# Revit family: Toilet_Seat-Round_Closed_Front-KOHLER-Stonewood-K-4648
name_source: partatom
category: Specialty Equipment
revit_build: Autodesk Revit 2015 (Build: 20140606_1530(x64)
units: mm (PartAtom-declared; Revit-internal decimal feet)

## types (3) — shared parameters
ADA Compliant = No
Assembly Code = C1030200
Date Modified = 12/20/2019
Default Elevation = 0"
Description = Round-Front Toilet Seat
Height = 1 1/16"
Length = 16 5/8"
Manufacturer = KOHLER Co.
MasterFormat 1995 = 10820
MasterFormat 2004 = 10.28.13
Material = Molded Wood
Product Documentation Link = https://www.us.kohler.com
Product Name = Stonewood
Product Page URL = http://www.us.kohler.com
URL = https://www.us.kohler.com
WaterSense Certified = No
Width = 14 3/16"

## per-type parameters (varying)
| type | Finish | Model | Type |
| 0-White | Kohler-Wood-Molded-0-White | K-4648-0 | 1 |
| 96-Biscuit | Kohler-Wood-Molded-96-Biscuit | K-4648-96 | 2 |
| 47-Almond | Kohler-Wood-Molded-47-Almond | K-4648-47 | 3 |

## geometry (parser evidence)
native form markers: Sweep x5
no freeform markers — native parametric forms only
